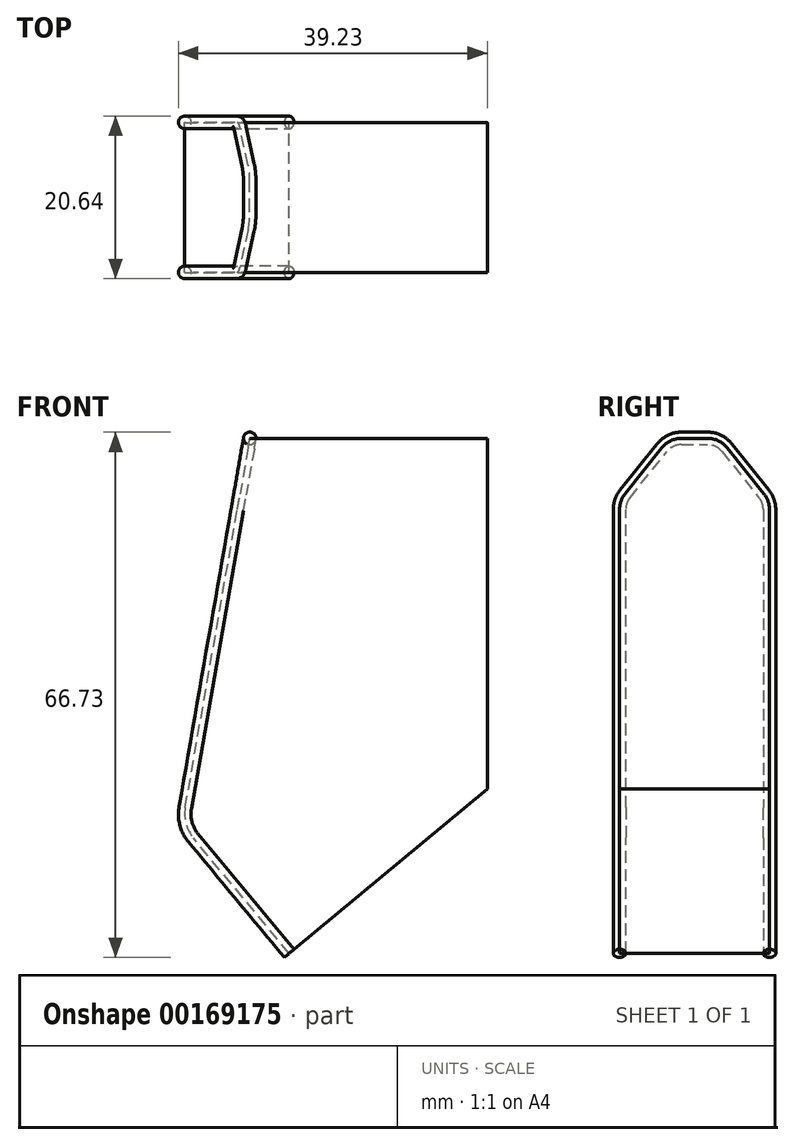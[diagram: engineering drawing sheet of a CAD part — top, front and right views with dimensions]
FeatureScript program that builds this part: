
annotation { "Feature Type Name" : "Feature", "Feature Type Description" : "" }
export const myFeature = defineFeature(function(context is Context, id is Id, definition is map)
    precondition{}
    {
        {
            var Q0;
            Q0=qCreatedBy(makeId("Front.planeOp"),FACE);
            var sketch = newSketch(context, id + "F0", { "sketchPlane" : qUnion([Q0])});
            skLineSegment(sketch, "E0", {"start": v(0, 0) * mm, "end": v(-12.18, 14.65) * mm});
            skLineSegment(sketch, "E1", {"start": v(-13.2, 18.51) * mm, "end": v(-5.01, 65.43) * mm});
            skLineSegment(sketch, "E2", {"start": v(-5.01, 65.43) * mm, "end": v(25.16, 65.43) * mm});
            skLineSegment(sketch, "E3", {"start": v(25.16, 65.43) * mm, "end": v(25.16, 20.92) * mm});
            skLineSegment(sketch, "E4", {"start": v(25.16, 20.92) * mm, "end": v(0, 0) * mm});
            skPoint(sketch, "E5.visualSharp", {"position": v(-13.59, 16.34) * mm});
            skArc(sketch, "E5.filletArc", {"start": v(-13.2, 18.51) * mm, "mid": v(-13.12, 16.47) * mm, "end": v(-12.18, 14.65) * mm});
            skPoint(sketch, "E6.orphan", {"position": v(25.16, 0) * mm});
            skSolve(sketch);
        }
        {
            var Q0;
            Q0=makeQuery(id+"F0.imprint","IMPRINT",FACE,{"disambiguationData":[TD([[makeQuery(id+"F0.imprint","IMPRINT",EDGE,{"derivedFrom":sQuery(id+"F0.wireOp",EDGE,"E0")}),-1.0]])]});
            extrude(context, id + "F1", {"entities" : qUnion([Q0]), "endBound" : BoundingType.SYMMETRIC, "depth" : 19.05 * mm});
        }
        {
            var Q0;
            Q0=makeQuery(id+"F1.opExtrude","SWEPT_FACE",FACE,{"disambiguationData":[OSD([sQuery(id+"F0.wireOp",EDGE,"E4")])]});
            var sketch = newSketch(context, id + "F2", { "sketchPlane" : qUnion([Q0])});
            skCircle(sketch, "E7", {"center": v(0, 9.53) * mm, "radius": 0.8 * mm});
            skSolve(sketch);
        }
        {
            var Q0;
            Q0=makeQuery(id+"F1.opExtrude","CAP_EDGE",EDGE,{"disambiguationData":[OSD([sQuery(id+"F0.wireOp",EDGE,"E2")])],"isStart":false});
            var Q1;
            Q1=makeQuery(id+"F1.opExtrude","CAP_EDGE",EDGE,{"disambiguationData":[OSD([sQuery(id+"F0.wireOp",EDGE,"E2")])],"isStart":true});
            chamfer(context, id + "F3", {"entities" : qUnion([Q0, Q1]), "chamferType" : ChamferType.TWO_OFFSETS, "width1" : 6.35 * mm, "oppositeDirection" : false, "width2" : 7.94 * mm, "tangentPropagation" : true});
        }
        {
            var Q0;
            {var subQ0=sQuery(id+"F0.wireOp",EDGE,"E2");Q0=makeQuery(id+"F3.opChamfer","BLEND_EDGE",EDGE,{"blendedFrom":[makeQuery(id+"F1.opExtrude","CAP_EDGE",EDGE,{"disambiguationData":[OSD([subQ0])],"isStart":true}),makeQuery(id+"F1.opExtrude","CAP_FACE",FACE,{"disambiguationData":[OSD([sQuery(id+"F0.wireOp",EDGE,"E0"),sQuery(id+"F0.wireOp",EDGE,"E1"),subQ0,sQuery(id+"F0.wireOp",EDGE,"E3"),sQuery(id+"F0.wireOp",EDGE,"E4"),sQuery(id+"F0.wireOp",EDGE,"E5.filletArc")])],"isStart":true})],"blendedInto":[makeQuery(id+"F1.opExtrude","CAP_FACE",FACE,{"disambiguationData":[OSD([sQuery(id+"F0.wireOp",EDGE,"E0"),sQuery(id+"F0.wireOp",EDGE,"E1"),subQ0,sQuery(id+"F0.wireOp",EDGE,"E3"),sQuery(id+"F0.wireOp",EDGE,"E4"),sQuery(id+"F0.wireOp",EDGE,"E5.filletArc")])],"isStart":true})]});}
            var Q1;
            {var subQ0=sQuery(id+"F0.wireOp",EDGE,"E2");Q1=makeQuery(id+"F3.opChamfer","BLEND_EDGE",EDGE,{"blendedFrom":[makeQuery(id+"F1.opExtrude","CAP_EDGE",EDGE,{"disambiguationData":[OSD([subQ0])],"isStart":true}),makeQuery(id+"F1.opExtrude","SWEPT_FACE",FACE,{"disambiguationData":[OSD([subQ0])]})],"blendedInto":[makeQuery(id+"F1.opExtrude","SWEPT_FACE",FACE,{"disambiguationData":[OSD([subQ0])]})]});}
            var Q2;
            {var subQ0=sQuery(id+"F0.wireOp",EDGE,"E2");Q2=makeQuery(id+"F3.opChamfer","BLEND_EDGE",EDGE,{"blendedFrom":[makeQuery(id+"F1.opExtrude","CAP_EDGE",EDGE,{"disambiguationData":[OSD([subQ0])],"isStart":false}),makeQuery(id+"F1.opExtrude","SWEPT_FACE",FACE,{"disambiguationData":[OSD([subQ0])]})],"blendedInto":[makeQuery(id+"F1.opExtrude","SWEPT_FACE",FACE,{"disambiguationData":[OSD([subQ0])]})]});}
            var Q3;
            {var subQ0=sQuery(id+"F0.wireOp",EDGE,"E2");Q3=makeQuery(id+"F3.opChamfer","BLEND_EDGE",EDGE,{"blendedFrom":[makeQuery(id+"F1.opExtrude","CAP_EDGE",EDGE,{"disambiguationData":[OSD([subQ0])],"isStart":false}),makeQuery(id+"F1.opExtrude","CAP_FACE",FACE,{"disambiguationData":[OSD([sQuery(id+"F0.wireOp",EDGE,"E0"),sQuery(id+"F0.wireOp",EDGE,"E1"),subQ0,sQuery(id+"F0.wireOp",EDGE,"E3"),sQuery(id+"F0.wireOp",EDGE,"E4"),sQuery(id+"F0.wireOp",EDGE,"E5.filletArc")])],"isStart":false})],"blendedInto":[makeQuery(id+"F1.opExtrude","CAP_FACE",FACE,{"disambiguationData":[OSD([sQuery(id+"F0.wireOp",EDGE,"E0"),sQuery(id+"F0.wireOp",EDGE,"E1"),subQ0,sQuery(id+"F0.wireOp",EDGE,"E3"),sQuery(id+"F0.wireOp",EDGE,"E4"),sQuery(id+"F0.wireOp",EDGE,"E5.filletArc")])],"isStart":false})]});}
            fillet(context, id + "F4", {"entities" : qUnion([Q0, Q1, Q2, Q3]), "radius" : 3.17 * mm, "tangentPropagation" : true, "allowEdgeOverflow" : false});
        }
        {
            var Q0;
            {var subQ0=sQuery(id+"F2.wireOp",EDGE,"E7");var subQ1=sQuery(id+"F0.wireOp",EDGE,"E4");var subQ4=makeQuery(id+"F1.opExtrude","CAP_EDGE",EDGE,{"disambiguationData":[OSD([subQ1])],"isStart":false});var subQ5=makeQuery(id+"F2.imprint","INTERSECT",VERTEX,{"derivedFrom":[subQ4,subQ0]});Q0=makeQuery(id+"F2.imprint","IMPRINT",FACE,{"disambiguationData":[TD([[makeQuery(id+"F2.imprint","IMPRINT",EDGE,{"disambiguationData":[TD([[subQ5,-1.0]])],"derivedFrom":subQ0}),1.0]])]});}
            var Q1;
            {var subQ0=sQuery(id+"F2.wireOp",EDGE,"E7");var subQ1=sQuery(id+"F0.wireOp",EDGE,"E4");var subQ4=makeQuery(id+"F1.opExtrude","CAP_EDGE",EDGE,{"disambiguationData":[OSD([subQ1])],"isStart":false});var subQ5=makeQuery(id+"F2.imprint","INTERSECT",VERTEX,{"derivedFrom":[subQ4,subQ0]});Q1=makeQuery(id+"F2.imprint","IMPRINT",FACE,{"disambiguationData":[TD([[makeQuery(id+"F2.imprint","IMPRINT",EDGE,{"disambiguationData":[TD([[subQ5,1.0]])],"derivedFrom":subQ0}),1.0]])]});}
            var Q2;
            Q2=makeQuery(id+"F1.opExtrude","CAP_EDGE",EDGE,{"disambiguationData":[OSD([sQuery(id+"F0.wireOp",EDGE,"E0")])],"isStart":false});
            var Q3;
            Q3=makeQuery(id+"F1.opExtrude","CAP_EDGE",EDGE,{"disambiguationData":[OSD([sQuery(id+"F0.wireOp",EDGE,"E5.filletArc")])],"isStart":false});
            var Q4;
            Q4=makeQuery(id+"F1.opExtrude","CAP_EDGE",EDGE,{"disambiguationData":[OSD([sQuery(id+"F0.wireOp",EDGE,"E1")])],"isStart":false});
            var Q5;
            {var subQ0=sQuery(id+"F0.wireOp",EDGE,"E1");var subQ1=sQuery(id+"F0.wireOp",EDGE,"E2");Q5=makeQuery(id+"F4.opFillet","BLEND_EDGE",EDGE,{"blendedFrom":[makeQuery(id+"F3.opChamfer","BLEND_EDGE",EDGE,{"blendedFrom":[makeQuery(id+"F1.opExtrude","CAP_EDGE",EDGE,{"disambiguationData":[OSD([subQ1])],"isStart":false}),makeQuery(id+"F1.opExtrude","CAP_FACE",FACE,{"disambiguationData":[OSD([sQuery(id+"F0.wireOp",EDGE,"E0"),subQ0,subQ1,sQuery(id+"F0.wireOp",EDGE,"E3"),sQuery(id+"F0.wireOp",EDGE,"E4"),sQuery(id+"F0.wireOp",EDGE,"E5.filletArc")])],"isStart":false})],"blendedInto":[makeQuery(id+"F1.opExtrude","CAP_FACE",FACE,{"disambiguationData":[OSD([sQuery(id+"F0.wireOp",EDGE,"E0"),subQ0,subQ1,sQuery(id+"F0.wireOp",EDGE,"E3"),sQuery(id+"F0.wireOp",EDGE,"E4"),sQuery(id+"F0.wireOp",EDGE,"E5.filletArc")])],"isStart":false})]}),makeQuery(id+"F1.opExtrude","SWEPT_FACE",FACE,{"disambiguationData":[OSD([subQ0])]})],"blendedInto":[makeQuery(id+"F1.opExtrude","SWEPT_FACE",FACE,{"disambiguationData":[OSD([subQ0])]})]});}
            var Q6;
            Q6=makeQuery(id+"F3.opChamfer","BLEND_EDGE",EDGE,{"blendedFrom":[makeQuery(id+"F1.opExtrude","CAP_EDGE",EDGE,{"disambiguationData":[OSD([sQuery(id+"F0.wireOp",EDGE,"E2")])],"isStart":false}),makeQuery(id+"F1.opExtrude","SWEPT_FACE",FACE,{"disambiguationData":[OSD([sQuery(id+"F0.wireOp",EDGE,"E1")])]})],"blendedInto":[makeQuery(id+"F1.opExtrude","SWEPT_FACE",FACE,{"disambiguationData":[OSD([sQuery(id+"F0.wireOp",EDGE,"E1")])]})]});
            var Q7;
            {var subQ0=sQuery(id+"F0.wireOp",EDGE,"E2");Q7=makeQuery(id+"F4.opFillet","BLEND_EDGE",EDGE,{"blendedFrom":[makeQuery(id+"F3.opChamfer","BLEND_EDGE",EDGE,{"blendedFrom":[makeQuery(id+"F1.opExtrude","CAP_EDGE",EDGE,{"disambiguationData":[OSD([subQ0])],"isStart":false}),makeQuery(id+"F1.opExtrude","SWEPT_FACE",FACE,{"disambiguationData":[OSD([subQ0])]})],"blendedInto":[makeQuery(id+"F1.opExtrude","SWEPT_FACE",FACE,{"disambiguationData":[OSD([subQ0])]})]}),makeQuery(id+"F1.opExtrude","SWEPT_FACE",FACE,{"disambiguationData":[OSD([sQuery(id+"F0.wireOp",EDGE,"E1")])]})],"blendedInto":[makeQuery(id+"F1.opExtrude","SWEPT_FACE",FACE,{"disambiguationData":[OSD([sQuery(id+"F0.wireOp",EDGE,"E1")])]})]});}
            var Q8;
            Q8=makeQuery(id+"F1.opExtrude","SWEPT_EDGE",EDGE,{"disambiguationData":[OSD([sQuery(id+"F0.wireOp",EDGE,"E1"),sQuery(id+"F0.wireOp",EDGE,"E2")])]});
            var Q9;
            {var subQ0=sQuery(id+"F0.wireOp",EDGE,"E2");Q9=makeQuery(id+"F4.opFillet","BLEND_EDGE",EDGE,{"blendedFrom":[makeQuery(id+"F3.opChamfer","BLEND_EDGE",EDGE,{"blendedFrom":[makeQuery(id+"F1.opExtrude","CAP_EDGE",EDGE,{"disambiguationData":[OSD([subQ0])],"isStart":true}),makeQuery(id+"F1.opExtrude","SWEPT_FACE",FACE,{"disambiguationData":[OSD([subQ0])]})],"blendedInto":[makeQuery(id+"F1.opExtrude","SWEPT_FACE",FACE,{"disambiguationData":[OSD([subQ0])]})]}),makeQuery(id+"F1.opExtrude","SWEPT_FACE",FACE,{"disambiguationData":[OSD([sQuery(id+"F0.wireOp",EDGE,"E1")])]})],"blendedInto":[makeQuery(id+"F1.opExtrude","SWEPT_FACE",FACE,{"disambiguationData":[OSD([sQuery(id+"F0.wireOp",EDGE,"E1")])]})]});}
            var Q10;
            Q10=makeQuery(id+"F3.opChamfer","BLEND_EDGE",EDGE,{"blendedFrom":[makeQuery(id+"F1.opExtrude","CAP_EDGE",EDGE,{"disambiguationData":[OSD([sQuery(id+"F0.wireOp",EDGE,"E2")])],"isStart":true}),makeQuery(id+"F1.opExtrude","SWEPT_FACE",FACE,{"disambiguationData":[OSD([sQuery(id+"F0.wireOp",EDGE,"E1")])]})],"blendedInto":[makeQuery(id+"F1.opExtrude","SWEPT_FACE",FACE,{"disambiguationData":[OSD([sQuery(id+"F0.wireOp",EDGE,"E1")])]})]});
            var Q11;
            {var subQ0=sQuery(id+"F0.wireOp",EDGE,"E1");var subQ1=sQuery(id+"F0.wireOp",EDGE,"E2");Q11=makeQuery(id+"F4.opFillet","BLEND_EDGE",EDGE,{"blendedFrom":[makeQuery(id+"F3.opChamfer","BLEND_EDGE",EDGE,{"blendedFrom":[makeQuery(id+"F1.opExtrude","CAP_EDGE",EDGE,{"disambiguationData":[OSD([subQ1])],"isStart":true}),makeQuery(id+"F1.opExtrude","CAP_FACE",FACE,{"disambiguationData":[OSD([sQuery(id+"F0.wireOp",EDGE,"E0"),subQ0,subQ1,sQuery(id+"F0.wireOp",EDGE,"E3"),sQuery(id+"F0.wireOp",EDGE,"E4"),sQuery(id+"F0.wireOp",EDGE,"E5.filletArc")])],"isStart":true})],"blendedInto":[makeQuery(id+"F1.opExtrude","CAP_FACE",FACE,{"disambiguationData":[OSD([sQuery(id+"F0.wireOp",EDGE,"E0"),subQ0,subQ1,sQuery(id+"F0.wireOp",EDGE,"E3"),sQuery(id+"F0.wireOp",EDGE,"E4"),sQuery(id+"F0.wireOp",EDGE,"E5.filletArc")])],"isStart":true})]}),makeQuery(id+"F1.opExtrude","SWEPT_FACE",FACE,{"disambiguationData":[OSD([subQ0])]})],"blendedInto":[makeQuery(id+"F1.opExtrude","SWEPT_FACE",FACE,{"disambiguationData":[OSD([subQ0])]})]});}
            var Q12;
            Q12=makeQuery(id+"F1.opExtrude","CAP_EDGE",EDGE,{"disambiguationData":[OSD([sQuery(id+"F0.wireOp",EDGE,"E1")])],"isStart":true});
            var Q13;
            Q13=makeQuery(id+"F1.opExtrude","CAP_EDGE",EDGE,{"disambiguationData":[OSD([sQuery(id+"F0.wireOp",EDGE,"E5.filletArc")])],"isStart":true});
            var Q14;
            Q14=makeQuery(id+"F1.opExtrude","CAP_EDGE",EDGE,{"disambiguationData":[OSD([sQuery(id+"F0.wireOp",EDGE,"E0")])],"isStart":true});
            sweep(context, id + "F5", {"profiles" : qUnion([Q0, Q1]), "path" : qUnion([Q2, Q3, Q4, Q5, Q6, Q7, Q8, Q9, Q10, Q11, Q12, Q13, Q14])});
        }
    });
